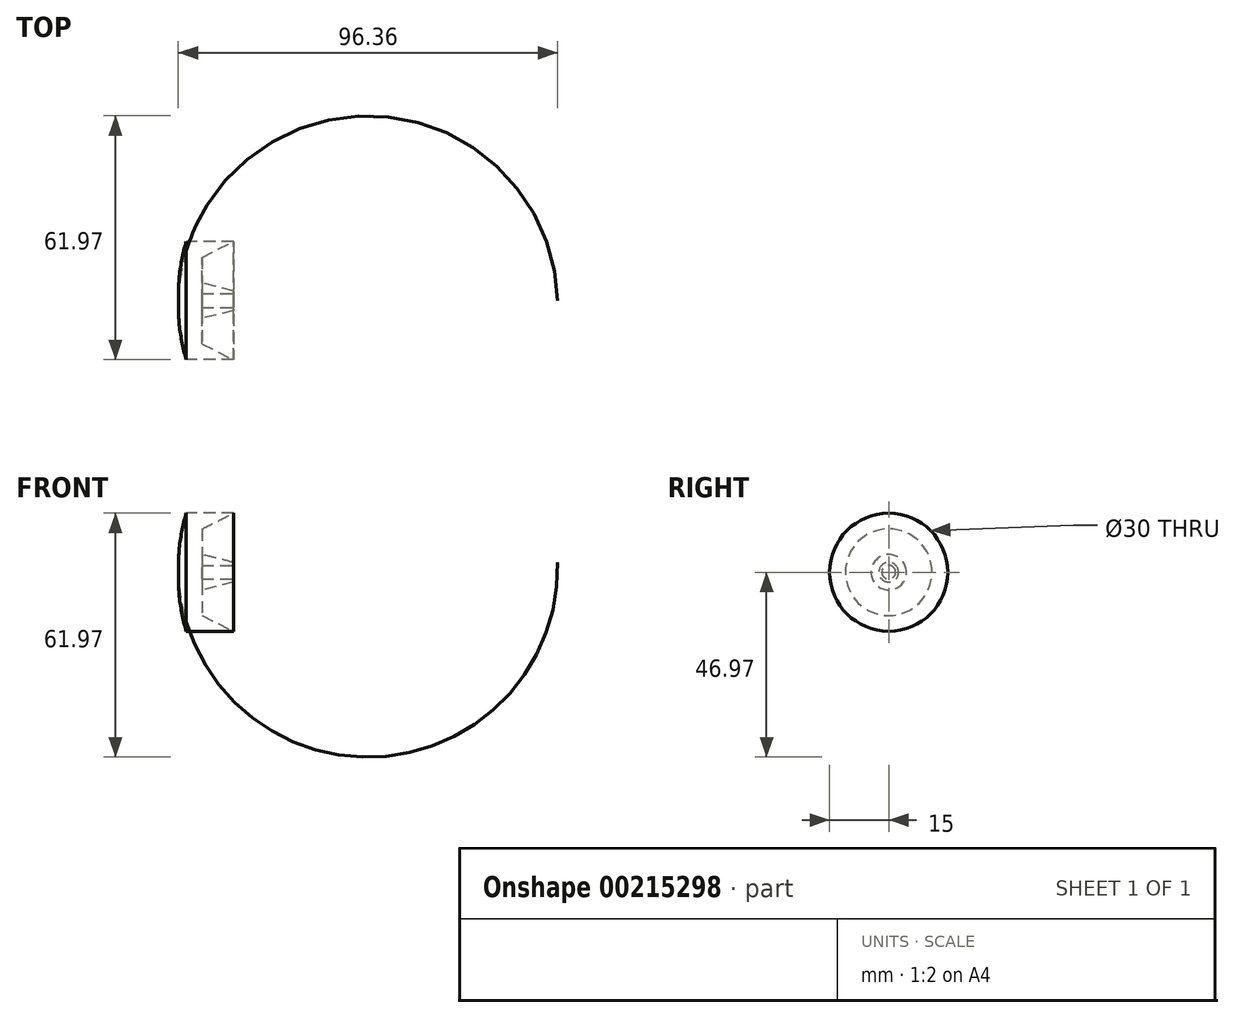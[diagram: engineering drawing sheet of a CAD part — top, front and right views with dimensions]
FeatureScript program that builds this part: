
annotation { "Feature Type Name" : "Feature", "Feature Type Description" : "" }
export const myFeature = defineFeature(function(context is Context, id is Id, definition is map)
    precondition{}
    {
        {
            var Q0;
            Q0=qCreatedBy(makeId("Top.planeOp"),FACE);
            var sketch = newSketch(context, id + "F0", { "sketchPlane" : qUnion([Q0])});
            skLineSegment(sketch, "E0", {"start": v(0, 15) * mm, "end": v(12, 15) * mm});
            skLineSegment(sketch, "E1", {"start": v(12, 15) * mm, "end": v(4, 11) * mm});
            skLineSegment(sketch, "E2", {"start": v(4, 11) * mm, "end": v(4, 4.5) * mm});
            skArc(sketch, "E3", {"start": v(0, 15) * mm, "mid": v(-1.6, 7.58) * mm, "end": v(-2, 0) * mm});
            skPoint(sketch, "E4.start.orphan", {"position": v(0, 0) * mm});
            skLineSegment(sketch, "E5", {"start": v(4, 4.5) * mm, "end": v(12, 2.5) * mm});
            skLineSegment(sketch, "E6", {"start": v(12, 2.5) * mm, "end": v(12, 0) * mm});
            skLineSegment(sketch, "E7", {"start": v(12, 0) * mm, "end": v(-2, 0) * mm});
            skLineSegment(sketch, "E8", {"start": v(-11.88, 0) * mm, "end": v(18.18, 0) * mm, "construction": true});
            skSolve(sketch);
        }
        {
            var Q0;
            Q0=makeQuery(id+"F0.imprint","IMPRINT",FACE,{"disambiguationData":[TD([[makeQuery(id+"F0.imprint","IMPRINT",EDGE,{"derivedFrom":sQuery(id+"F0.wireOp",EDGE,"E0")}),-1.0]])]});
            var Q1;
            Q1=sQuery(id+"F0.wireOp",EDGE,"E8");
            revolve(context, id + "F1", {"entities" : qUnion([Q0]), "axis" : qUnion([Q1]), "revolveType" : RevolveType.FULL});
        }
        {
            var Q0;
            Q0=makeQuery(id+"F1.opRevolve","SWEPT_FACE",FACE,{"disambiguationData":[OSD([sQuery(id+"F0.wireOp",EDGE,"E6")])]});
            var sketch = newSketch(context, id + "F2", { "sketchPlane" : qUnion([Q0])});
            skCircle(sketch, "E9", {"center": v(0, 0) * mm, "radius": 1.75 * mm});
            skSolve(sketch);
        }
        {
            var Q0;
            Q0=makeQuery(id+"F2.imprint","IMPRINT",FACE,{"disambiguationData":[TD([[makeQuery(id+"F2.imprint","IMPRINT",EDGE,{"derivedFrom":sQuery(id+"F2.wireOp",EDGE,"E9")}),1.0]])]});
            extrude(context, id + "F3", {"entities" : qUnion([Q0]), "operationType" : NewBodyOperationType.REMOVE, "oppositeDirection" : true, "depth" : 8 * mm});
        }
    });
